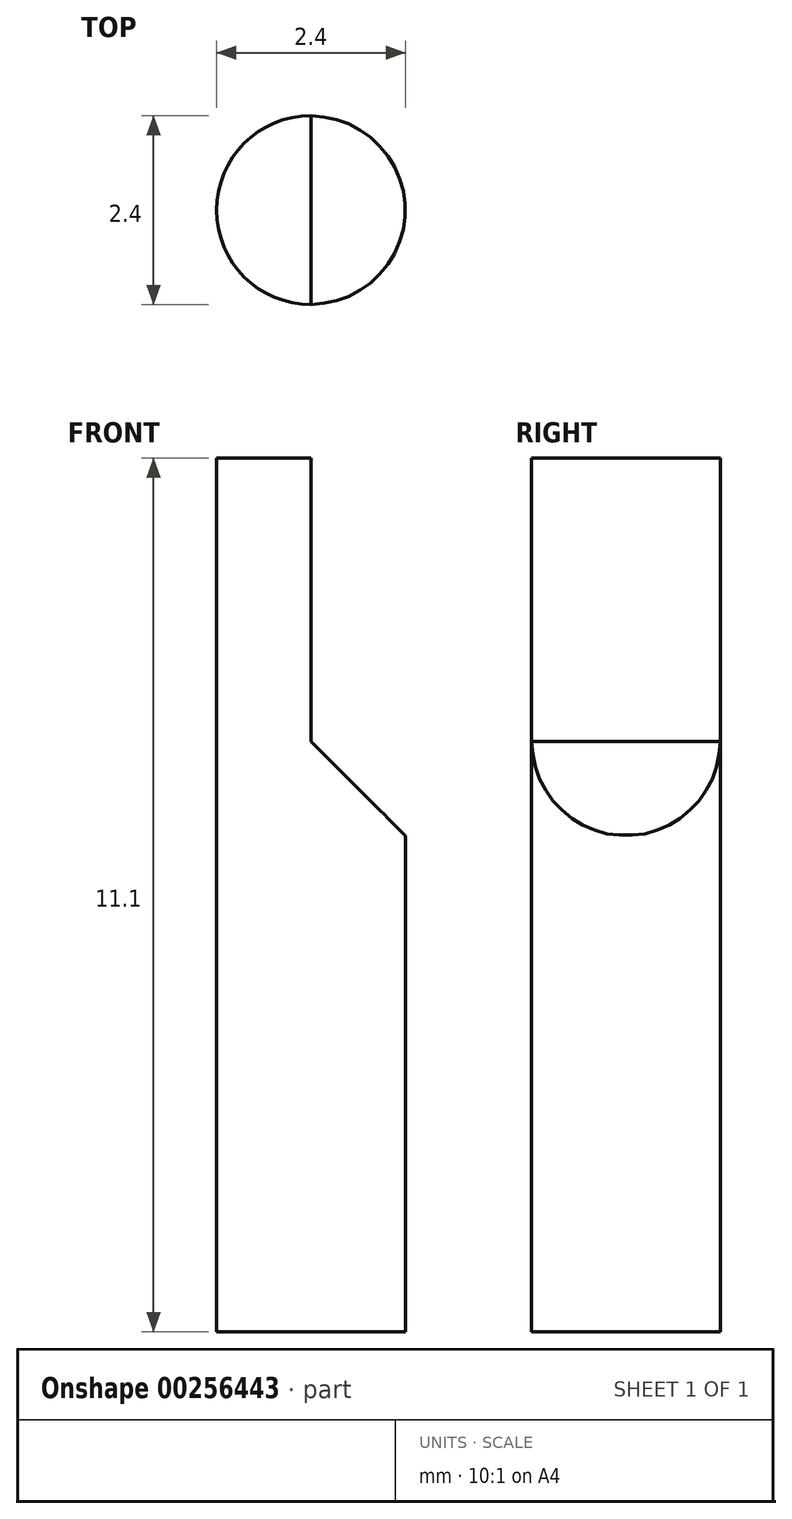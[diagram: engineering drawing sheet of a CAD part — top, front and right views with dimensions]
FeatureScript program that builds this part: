
annotation { "Feature Type Name" : "Feature", "Feature Type Description" : "" }
export const myFeature = defineFeature(function(context is Context, id is Id, definition is map)
    precondition{}
    {
        {
            var Q0;
            Q0=qCreatedBy(makeId("Top.planeOp"),FACE);
            var sketch = newSketch(context, id + "F0", { "sketchPlane" : qUnion([Q0])});
            skCircle(sketch, "E0", {"center": v(0, 0) * mm, "radius": 0.4 * mm});
            skSolve(sketch);
        }
        {
            var Q0;
            Q0=makeQuery(id+"F0.imprint","IMPRINT",FACE,{"disambiguationData":[TD([[makeQuery(id+"F0.imprint","IMPRINT",EDGE,{"derivedFrom":sQuery(id+"F0.wireOp",EDGE,"E0")}),1.0]])]});
            extrude(context, id + "F1", {"entities" : qUnion([Q0]), "depth" : 3.7 * mm});
        }
        {
            var Q0;
            Q0=makeQuery(id+"F1.opExtrude","SWEPT_BODY",BODY,{"disambiguationData":[OSD([sQuery(id+"F0.wireOp",EDGE,"E0")])]});
            transform(context, id + "F2", {"entities" : qUnion([Q0]), "transformType" : TransformType.TRANSLATION_3D, "dx" : 0 * mm, "dy" : 0 * mm, "dz" : 0 * mm, "makeCopy" : true});
        }
        {
            var Q0;
            Q0=qCreatedBy(makeId("Front.planeOp"),FACE);
            var sketch = newSketch(context, id + "F3", { "sketchPlane" : qUnion([Q0])});
            skLineSegment(sketch, "E1", {"start": v(0, 0) * mm, "end": v(0, 3.7) * mm, "construction": true});
            skLineSegment(sketch, "E2", {"start": v(0, 3.7) * mm, "end": v(0, 2.5) * mm});
            skLineSegment(sketch, "E3", {"start": v(0, 2.5) * mm, "end": v(0.4, 2.1) * mm});
            skLineSegment(sketch, "E4", {"start": v(0.4, 2.1) * mm, "end": v(0.4, 3.7) * mm});
            skLineSegment(sketch, "E5", {"start": v(0.4, 3.7) * mm, "end": v(0, 3.7) * mm});
            skSolve(sketch);
        }
        {
            var Q0;
            Q0=makeQuery(id+"F3.imprint","IMPRINT",FACE,{"disambiguationData":[TD([[makeQuery(id+"F3.imprint","IMPRINT",EDGE,{"derivedFrom":sQuery(id+"F3.wireOp",EDGE,"E2")}),1.0]])]});
            extrude(context, id + "F4", {"entities" : qUnion([Q0]), "operationType" : NewBodyOperationType.REMOVE, "oppositeDirection" : true, "depth" : 1 * mm, "symmetric" : true});
        }
        {
            var Q0;
            Q0=makeQuery(id+"F1.opExtrude","SWEPT_BODY",BODY,{"disambiguationData":[OSD([sQuery(id+"F0.wireOp",EDGE,"E0")])]});
            var Q1;
            Q1=makeQuery(id+"F2.opPattern","COPY",BODY,{"derivedFrom":makeQuery(id+"F1.opExtrude","SWEPT_BODY",BODY,{"disambiguationData":[OSD([sQuery(id+"F0.wireOp",EDGE,"E0")])]}),"instanceName":"1"});
            var Q2;
            Q2=qCreatedBy(makeId("Origin.pointOp"),VERTEX);
            transform(context, id + "F5", {"entities" : qUnion([Q0, Q1]), "transformType" : TransformType.SCALE_UNIFORMLY, "scale" : 3, "makeCopy" : false, "scalePoint" : qUnion([Q2])});
        }
    });
